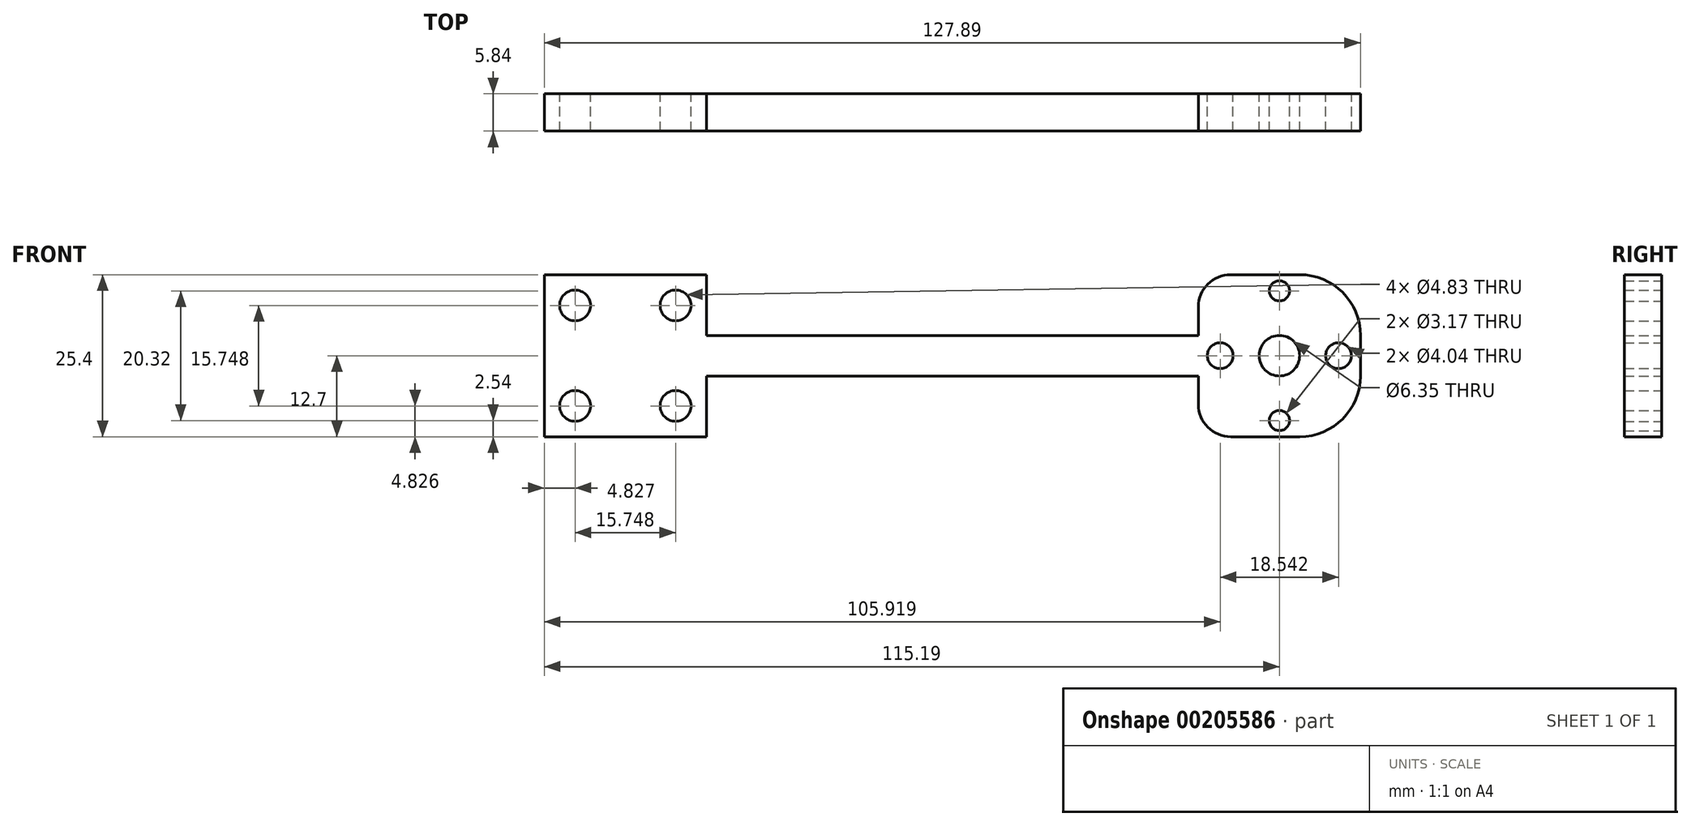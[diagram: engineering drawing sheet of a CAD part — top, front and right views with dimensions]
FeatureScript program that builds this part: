
annotation { "Feature Type Name" : "Feature", "Feature Type Description" : "" }
export const myFeature = defineFeature(function(context is Context, id is Id, definition is map)
    precondition{}
    {
        {
            var Q0;
            Q0=qCreatedBy(makeId("Front.planeOp"),FACE);
            var sketch = newSketch(context, id + "F0", { "sketchPlane" : qUnion([Q0])});
            skLineSegment(sketch, "E0.bottom", {"start": v(-12.7, 12.7) * mm, "end": v(12.7, 12.7) * mm});
            skLineSegment(sketch, "E0.top", {"start": v(-12.7, -12.7) * mm, "end": v(12.7, -12.7) * mm});
            skLineSegment(sketch, "E0.left", {"start": v(-12.7, 12.7) * mm, "end": v(-12.7, -12.7) * mm});
            skLineSegment(sketch, "E0.right", {"start": v(12.7, 12.7) * mm, "end": v(12.7, -12.7) * mm});
            skPoint(sketch, "E0.middle", {"position": v(0, 0) * mm});
            skLineSegment(sketch, "E1.bottom", {"start": v(-115.19, 12.7) * mm, "end": v(-89.79, 12.7) * mm});
            skLineSegment(sketch, "E1.top", {"start": v(-115.19, -12.7) * mm, "end": v(-89.79, -12.7) * mm});
            skLineSegment(sketch, "E1.left", {"start": v(-115.19, 12.7) * mm, "end": v(-115.19, -12.7) * mm});
            skLineSegment(sketch, "E1.right", {"start": v(-89.79, 12.7) * mm, "end": v(-89.79, -12.7) * mm});
            skPoint(sketch, "E1.middle", {"position": v(-102.49, 0) * mm});
            skLineSegment(sketch, "E2", {"start": v(-89.79, 3.18) * mm, "end": v(-12.7, 3.18) * mm});
            skLineSegment(sketch, "E3", {"start": v(-89.79, -3.18) * mm, "end": v(-12.7, -3.18) * mm});
            skCircle(sketch, "E4", {"center": v(-110.36, 7.87) * mm, "radius": 2.41 * mm});
            skCircle(sketch, "E5", {"center": v(-94.62, 7.87) * mm, "radius": 2.41 * mm});
            skCircle(sketch, "E6", {"center": v(-110.36, -7.87) * mm, "radius": 2.41 * mm});
            skCircle(sketch, "E7", {"center": v(-94.62, -7.87) * mm, "radius": 2.41 * mm});
            skCircle(sketch, "E8", {"center": v(-9.27, 0) * mm, "radius": 2.02 * mm});
            skPoint(sketch, "E8.centerSnap0", {"position": v(-12.7, 0) * mm});
            skCircle(sketch, "E9", {"center": v(9.27, 0) * mm, "radius": 2.02 * mm});
            skCircle(sketch, "E10", {"center": v(0, 10.16) * mm, "radius": 1.59 * mm});
            skCircle(sketch, "E11", {"center": v(0, -10.16) * mm, "radius": 1.59 * mm});
            skCircle(sketch, "E12", {"center": v(0, 0) * mm, "radius": 3.18 * mm});
            skSolve(sketch);
        }
        {
            var Q0;
            Q0=qSketchRegion(id+"F0",true);
            extrude(context, id + "F1", {"entities" : qUnion([Q0]), "depth" : 5.84 * mm});
        }
        {
            var Q0;
            Q0=makeQuery(id+"F1.opExtrude","SWEPT_EDGE",EDGE,{"disambiguationData":[OSD([sQuery(id+"F0.wireOp",EDGE,"E0.bottom"),sQuery(id+"F0.wireOp",EDGE,"E0.right")])]});
            var Q1;
            Q1=makeQuery(id+"F1.opExtrude","SWEPT_EDGE",EDGE,{"disambiguationData":[OSD([sQuery(id+"F0.wireOp",EDGE,"E0.top"),sQuery(id+"F0.wireOp",EDGE,"E0.right")])]});
            fillet(context, id + "F2", {"entities" : qUnion([Q0, Q1]), "radius" : 9.52 * mm, "tangentPropagation" : true, "allowEdgeOverflow" : false});
        }
        {
            var Q0;
            Q0=makeQuery(id+"F1.opExtrude","SWEPT_EDGE",EDGE,{"disambiguationData":[OSD([sQuery(id+"F0.wireOp",EDGE,"E0.top"),sQuery(id+"F0.wireOp",EDGE,"E0.left")])]});
            var Q1;
            Q1=makeQuery(id+"F1.opExtrude","SWEPT_EDGE",EDGE,{"disambiguationData":[OSD([sQuery(id+"F0.wireOp",EDGE,"E0.bottom"),sQuery(id+"F0.wireOp",EDGE,"E0.left")])]});
            fillet(context, id + "F3", {"entities" : qUnion([Q0, Q1]), "radius" : 5.08 * mm, "tangentPropagation" : true, "allowEdgeOverflow" : false});
        }
    });
